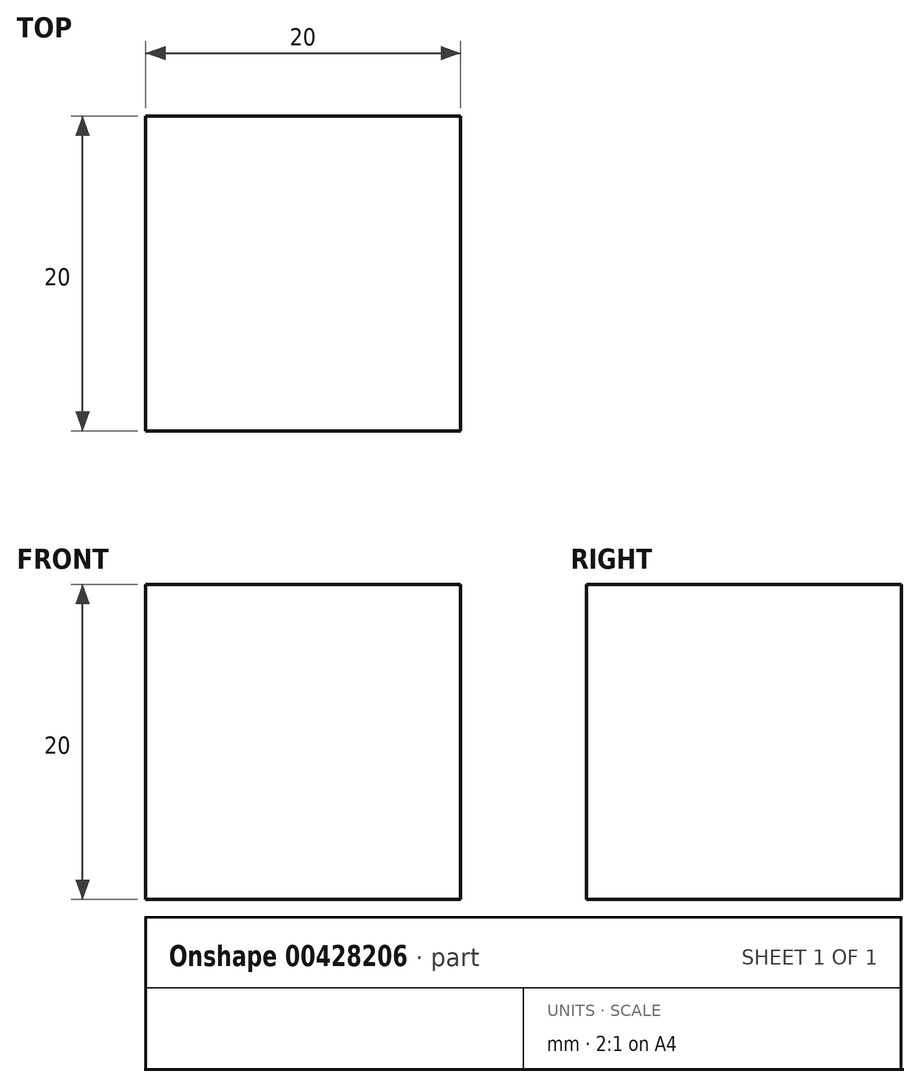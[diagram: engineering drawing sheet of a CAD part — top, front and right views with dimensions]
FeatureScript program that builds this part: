
annotation { "Feature Type Name" : "Feature", "Feature Type Description" : "" }
export const myFeature = defineFeature(function(context is Context, id is Id, definition is map)
    precondition{}
    {
        {
            var Q0;
            Q0=qCreatedBy(makeId("Front.planeOp"),FACE);
            var sketch = newSketch(context, id + "F0", { "sketchPlane" : qUnion([Q0])});
            skLineSegment(sketch, "E0.bottom", {"start": v(-6.63, 13.46) * mm, "end": v(13.37, 13.46) * mm});
            skLineSegment(sketch, "E0.top", {"start": v(-6.63, -6.54) * mm, "end": v(13.37, -6.54) * mm});
            skLineSegment(sketch, "E0.left", {"start": v(-6.63, 13.46) * mm, "end": v(-6.63, -6.54) * mm});
            skLineSegment(sketch, "E0.right", {"start": v(13.37, 13.46) * mm, "end": v(13.37, -6.54) * mm});
            skSolve(sketch);
        }
        {
            var Q0;
            Q0 = qSketchRegion(id + "F0", true);
            extrude(context, id + "F1", {"entities" : qUnion([Q0]), "depth" : 20 * mm});
        }
    });
